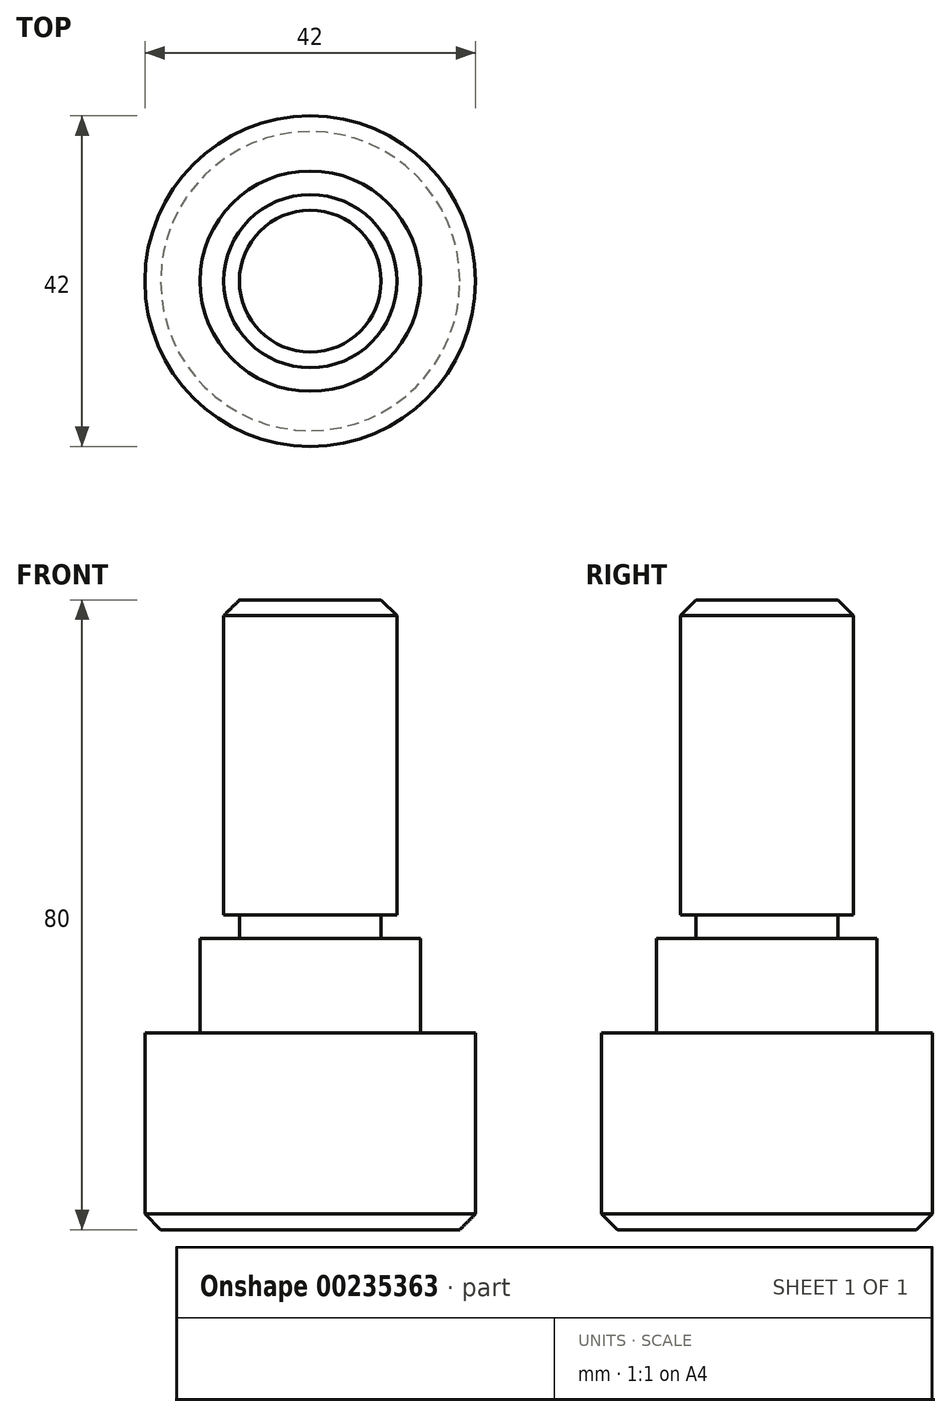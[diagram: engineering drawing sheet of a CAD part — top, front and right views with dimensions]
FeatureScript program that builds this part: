
annotation { "Feature Type Name" : "Feature", "Feature Type Description" : "" }
export const myFeature = defineFeature(function(context is Context, id is Id, definition is map)
    precondition{}
    {
        {
            var Q0;
            Q0=qCreatedBy(makeId("Front.planeOp"),FACE);
            var sketch = newSketch(context, id + "F0", { "sketchPlane" : qUnion([Q0])});
            skLineSegment(sketch, "E0", {"start": v(0, 0) * mm, "end": v(21, 0) * mm});
            skLineSegment(sketch, "E1", {"start": v(21, 0) * mm, "end": v(21, 25) * mm});
            skLineSegment(sketch, "E2", {"start": v(21, 25) * mm, "end": v(14, 25) * mm});
            skLineSegment(sketch, "E3", {"start": v(14, 25) * mm, "end": v(14, 37) * mm});
            skLineSegment(sketch, "E4", {"start": v(14, 37) * mm, "end": v(9, 37) * mm});
            skLineSegment(sketch, "E5", {"start": v(9, 37) * mm, "end": v(9, 40) * mm});
            skLineSegment(sketch, "E6", {"start": v(9, 40) * mm, "end": v(11, 40) * mm});
            skLineSegment(sketch, "E7", {"start": v(11, 40) * mm, "end": v(11, 80) * mm});
            skLineSegment(sketch, "E8", {"start": v(11, 80) * mm, "end": v(0, 80) * mm});
            skLineSegment(sketch, "E9", {"start": v(0, 80) * mm, "end": v(0, 0) * mm});
            skSolve(sketch);
        }
        {
            var Q0;
            Q0=makeQuery(id+"F0.imprint","IMPRINT",FACE,{"disambiguationData":[TD([[makeQuery(id+"F0.imprint","IMPRINT",EDGE,{"derivedFrom":sQuery(id+"F0.wireOp",EDGE,"E0")}),1.0]])]});
            var Q1;
            Q1=sQuery(id+"F0.wireOp",EDGE,"E9");
            revolve(context, id + "F1", {"entities" : qUnion([Q0]), "axis" : qUnion([Q1]), "revolveType" : RevolveType.FULL});
        }
        {
            var Q0;
            Q0=makeQuery(id+"F1.opRevolve","SWEPT_EDGE",EDGE,{"disambiguationData":[OSD([sQuery(id+"F0.wireOp",EDGE,"E7"),sQuery(id+"F0.wireOp",EDGE,"E8")])]});
            var Q1;
            Q1=makeQuery(id+"F1.opRevolve","SWEPT_EDGE",EDGE,{"disambiguationData":[OSD([sQuery(id+"F0.wireOp",EDGE,"E0"),sQuery(id+"F0.wireOp",EDGE,"E1")])]});
            chamfer(context, id + "F2", {"entities" : qUnion([Q0, Q1]), "chamferType" : ChamferType.OFFSET_ANGLE, "width" : 2 * mm, "oppositeDirection" : false, "angle" : 45 * degree, "tangentPropagation" : true});
        }
    });
